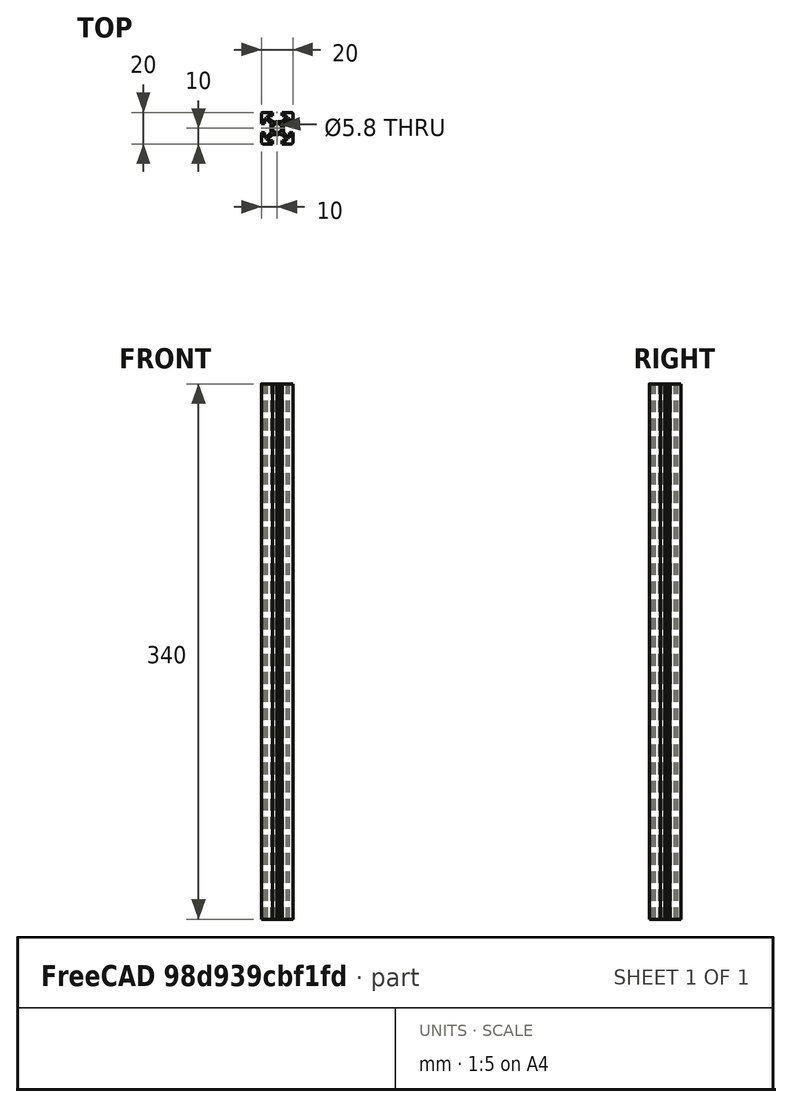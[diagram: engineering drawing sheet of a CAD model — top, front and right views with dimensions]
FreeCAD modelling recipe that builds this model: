
FCSTD DOCUMENT  (FreeCAD 0.17R13387 (Git))
Label: X-Profile_2020
License: All rights reserved
LicenseURL: http://en.wikipedia.org/wiki/All_rights_reserved
objects: Sketcher::SketchObject×1, PartDesign::Pad×1, PartDesign::Body×1
note: 4 computed .brp shape members not serialized (recipe doc carries the construction recipe); baked Part::Feature solids carry a one-line shape summary decoded from their .brp

FEATURE [Sketcher::SketchObject] Sketch001
  sketch-geometry (77):
    g0: LineSegment StartX=-8 StartY=-3 StartZ=0 EndX=-10 EndY=-3 EndZ=0
    g1: LineSegment StartX=-10 StartY=-3 StartZ=0 EndX=-10 EndY=-9 EndZ=0
    g2: ArcOfCircle CenterX=-9 CenterY=-9 CenterZ=0 NormalX=0 NormalY=0 NormalZ=1 AngleXU=0 Radius=1 StartAngle=3.14159 EndAngle=4.71239
    g3: LineSegment StartX=-9 StartY=-10 StartZ=0 EndX=-3 EndY=-10 EndZ=0
    g4: LineSegment StartX=-3 StartY=-10 StartZ=0 EndX=-3 EndY=-8 EndZ=0
    g5: LineSegment StartX=-3 StartY=-8 StartZ=0 EndX=-6 EndY=-8 EndZ=0
    g6: LineSegment StartX=-6 StartY=-8 StartZ=0 EndX=-6 EndY=-7.06066 EndZ=0
    g7: LineSegment StartX=-6 StartY=-7.06066 StartZ=0 EndX=-2.93934 EndY=-4 EndZ=0
    g8: LineSegment StartX=-2.93934 StartY=-4 StartZ=0 EndX=-0.65359 EndY=-4 EndZ=0
    g9: ArcOfCircle CenterX=-0.65359 CenterY=-3.5 CenterZ=0 NormalX=0 NormalY=0 NormalZ=1 AngleXU=0 Radius=0.5 StartAngle=4.71239 EndAngle=5.23599
    g10: LineSegment StartX=-0.40359 StartY=-3.93301 StartZ=0 EndX=0 EndY=-3.7 EndZ=0
    g11: LineSegment StartX=0 StartY=-3.7 StartZ=0 EndX=0.40359 EndY=-3.93301 EndZ=0
    g12: ArcOfCircle CenterX=0.65359 CenterY=-3.5 CenterZ=0 NormalX=0 NormalY=0 NormalZ=1 AngleXU=0 Radius=0.5 StartAngle=4.18879 EndAngle=5.23599
    g13: LineSegment StartX=0.90359 StartY=-3.93301 StartZ=0 EndX=1.21889 EndY=-3.75098 EndZ=0
    g14: LineSegment StartX=1.21889 StartY=-3.75098 StartZ=0 EndX=2.5 EndY=-4 EndZ=0
    g15: LineSegment StartX=2.5 StartY=-4 StartZ=0 EndX=2.93934 EndY=-4 EndZ=0
    g16: LineSegment StartX=2.93934 StartY=-4 StartZ=0 EndX=6 EndY=-7.06066 EndZ=0
    g17: LineSegment StartX=6 StartY=-7.06066 StartZ=0 EndX=6 EndY=-8 EndZ=0
    g18: LineSegment StartX=6 StartY=-8 StartZ=0 EndX=3 EndY=-8 EndZ=0
    g19: LineSegment StartX=3 StartY=-8 StartZ=0 EndX=3 EndY=-10 EndZ=0
    g20: LineSegment StartX=3 StartY=-10 StartZ=0 EndX=9 EndY=-10 EndZ=0
    g21: ArcOfCircle CenterX=9 CenterY=-9 CenterZ=0 NormalX=0 NormalY=0 NormalZ=1 AngleXU=0 Radius=1 StartAngle=4.71239 EndAngle=6.28319
    g22: LineSegment StartX=10 StartY=-9 StartZ=0 EndX=10 EndY=-3 EndZ=0
    g23: LineSegment StartX=10 StartY=-3 StartZ=0 EndX=8 EndY=-3 EndZ=0
    g24: LineSegment StartX=8 StartY=-3 StartZ=0 EndX=8 EndY=-6 EndZ=0
    g25: LineSegment StartX=8 StartY=-6 StartZ=0 EndX=7.06066 EndY=-6 EndZ=0
    g26: LineSegment StartX=7.06066 StartY=-6 StartZ=0 EndX=4 EndY=-2.93934 EndZ=0
    g27: LineSegment StartX=4 StartY=-2.93934 StartZ=0 EndX=4 EndY=-0.65359 EndZ=0
    g28: ArcOfCircle CenterX=3.5 CenterY=-0.65359 CenterZ=0 NormalX=0 NormalY=0 NormalZ=1 AngleXU=0 Radius=0.5 StartAngle=0 EndAngle=0.523599
    g29: LineSegment StartX=3.93301 StartY=-0.40359 StartZ=0 EndX=3.7 EndY=0 EndZ=0
    g30: LineSegment StartX=3.7 StartY=0 StartZ=0 EndX=3.93301 EndY=0.40359 EndZ=0
    g31: ArcOfCircle CenterX=3.5 CenterY=0.65359 CenterZ=0 NormalX=0 NormalY=0 NormalZ=1 AngleXU=0 Radius=0.5 StartAngle=5.75959 EndAngle=6.80678
    g32: LineSegment StartX=3.93301 StartY=0.90359 StartZ=0 EndX=3.75098 EndY=1.21889 EndZ=0
    g33: LineSegment StartX=3.75098 StartY=1.21889 StartZ=0 EndX=4 EndY=2.5 EndZ=0
    g34: LineSegment StartX=4 StartY=2.5 StartZ=0 EndX=4 EndY=2.93934 EndZ=0
    g35: LineSegment StartX=4 StartY=2.93934 StartZ=0 EndX=7.06066 EndY=6 EndZ=0
    g36: LineSegment StartX=7.06066 StartY=6 StartZ=0 EndX=8 EndY=6 EndZ=0
    g37: LineSegment StartX=8 StartY=6 StartZ=0 EndX=8 EndY=3 EndZ=0
    g38: LineSegment StartX=8 StartY=3 StartZ=0 EndX=10 EndY=3 EndZ=0
    g39: LineSegment StartX=10 StartY=3 StartZ=0 EndX=10 EndY=9 EndZ=0
    g40: ArcOfCircle CenterX=9 CenterY=9 CenterZ=0 NormalX=0 NormalY=0 NormalZ=1 AngleXU=0 Radius=1 StartAngle=0 EndAngle=1.5708
    g41: LineSegment StartX=9 StartY=10 StartZ=0 EndX=3 EndY=10 EndZ=0
    g42: LineSegment StartX=3 StartY=10 StartZ=0 EndX=3 EndY=8 EndZ=0
    g43: LineSegment StartX=3 StartY=8 StartZ=0 EndX=6 EndY=8 EndZ=0
    g44: LineSegment StartX=6 StartY=8 StartZ=0 EndX=6 EndY=7.06066 EndZ=0
    g45: LineSegment StartX=6 StartY=7.06066 StartZ=0 EndX=2.93934 EndY=4 EndZ=0
    g46: LineSegment StartX=2.93934 StartY=4 StartZ=0 EndX=0.65359 EndY=4 EndZ=0
    g47: ArcOfCircle CenterX=0.65359 CenterY=3.5 CenterZ=0 NormalX=0 NormalY=0 NormalZ=1 AngleXU=0 Radius=0.5 StartAngle=1.5708 EndAngle=2.0944
    g48: LineSegment StartX=0.40359 StartY=3.93301 StartZ=0 EndX=0 EndY=3.7 EndZ=0
    g49: LineSegment StartX=0 StartY=3.7 StartZ=0 EndX=-0.40359 EndY=3.93301 EndZ=0
    g50: ArcOfCircle CenterX=-0.65359 CenterY=3.5 CenterZ=0 NormalX=0 NormalY=0 NormalZ=1 AngleXU=0 Radius=0.5 StartAngle=1.0472 EndAngle=2.0944
    g51: LineSegment StartX=-0.90359 StartY=3.93301 StartZ=0 EndX=-1.21889 EndY=3.75098 EndZ=0
    g52: LineSegment StartX=-1.21889 StartY=3.75098 StartZ=0 EndX=-2.5 EndY=4 EndZ=0
    g53: LineSegment StartX=-2.5 StartY=4 StartZ=0 EndX=-2.93934 EndY=4 EndZ=0
    g54: LineSegment StartX=-2.93934 StartY=4 StartZ=0 EndX=-6 EndY=7.06066 EndZ=0
    g55: LineSegment StartX=-6 StartY=7.06066 StartZ=0 EndX=-6 EndY=8 EndZ=0
    g56: LineSegment StartX=-6 StartY=8 StartZ=0 EndX=-3 EndY=8 EndZ=0
    g57: LineSegment StartX=-3 StartY=8 StartZ=0 EndX=-3 EndY=10 EndZ=0
    g58: LineSegment StartX=-3 StartY=10 StartZ=0 EndX=-9 EndY=10 EndZ=0
    g59: ArcOfCircle CenterX=-9 CenterY=9 CenterZ=0 NormalX=0 NormalY=0 NormalZ=1 AngleXU=0 Radius=1 StartAngle=1.5708 EndAngle=3.14159
    g60: LineSegment StartX=-10 StartY=9 StartZ=0 EndX=-10 EndY=3 EndZ=0
    g61: LineSegment StartX=-10 StartY=3 StartZ=0 EndX=-8 EndY=3 EndZ=0
    g62: LineSegment StartX=-8 StartY=3 StartZ=0 EndX=-8 EndY=6 EndZ=0
    g63: LineSegment StartX=-8 StartY=6 StartZ=0 EndX=-7.06066 EndY=6 EndZ=0
    g64: LineSegment StartX=-7.06066 StartY=6 StartZ=0 EndX=-4 EndY=2.93934 EndZ=0
    g65: LineSegment StartX=-4 StartY=2.93934 StartZ=0 EndX=-4 EndY=0.65359 EndZ=0
    g66: ArcOfCircle CenterX=-3.5 CenterY=0.65359 CenterZ=0 NormalX=0 NormalY=0 NormalZ=1 AngleXU=0 Radius=0.5 StartAngle=3.14159 EndAngle=3.66519
    g67: LineSegment StartX=-3.93301 StartY=0.40359 StartZ=0 EndX=-3.7 EndY=0 EndZ=0
    g68: LineSegment StartX=-3.7 StartY=0 StartZ=0 EndX=-3.93301 EndY=-0.40359 EndZ=0
    g69: ArcOfCircle CenterX=-3.5 CenterY=-0.65359 CenterZ=0 NormalX=0 NormalY=0 NormalZ=1 AngleXU=0 Radius=0.5 StartAngle=2.61799 EndAngle=3.66519
    g70: LineSegment StartX=-3.93301 StartY=-0.90359 StartZ=0 EndX=-3.75098 EndY=-1.21889 EndZ=0
    g71: LineSegment StartX=-3.75098 StartY=-1.21889 StartZ=0 EndX=-4 EndY=-2.5 EndZ=0
    g72: LineSegment StartX=-4 StartY=-2.5 StartZ=0 EndX=-4 EndY=-2.93934 EndZ=0
    g73: LineSegment StartX=-4 StartY=-2.93934 StartZ=0 EndX=-7.06066 EndY=-6 EndZ=0
    g74: LineSegment StartX=-7.06066 StartY=-6 StartZ=0 EndX=-8 EndY=-6 EndZ=0
    g75: LineSegment StartX=-8 StartY=-6 StartZ=0 EndX=-8 EndY=-3 EndZ=0
    g76: Circle CenterX=0 CenterY=0 CenterZ=0 NormalX=0 NormalY=0 NormalZ=1 AngleXU=0 Radius=2.9
  constraints (105):
    c: Horizontal(g0)
    c: Coincident(g0,g1)
    c: Vertical(g1)
    c: Coincident(g1,g2)
    c: Coincident(g2,g3)
    c: Horizontal(g3)
    c: Coincident(g3,g4)
    c: Coincident(g4,g5)
    c: Horizontal(g5)
    c: Coincident(g5,g6)
    c: Coincident(g6,g7)
    c: Coincident(g7,g8)
    c: Horizontal(g8)
    c: Coincident(g8,g9)
    c: Coincident(g9,g10)
    c: Coincident(g10,g11)
    c: Coincident(g11,g12)
    c: Coincident(g12,g13)
    c: Coincident(g13,g14)
    c: Coincident(g14,g15)
    c: Horizontal(g15)
    c: Coincident(g15,g16)
    c: Coincident(g16,g17)
    c: Coincident(g17,g18)
    c: Coincident(g18,g19)
    c: Vertical(g19)
    c: Coincident(g19,g20)
    c: Horizontal(g20)
    c: Coincident(g20,g21)
    c: Coincident(g21,g22)
    c: Vertical(g22)
    c: Coincident(g22,g23)
    c: Horizontal(g23)
    c: Coincident(g23,g24)
    c: Vertical(g24)
    c: Coincident(g24,g25)
    c: Coincident(g25,g26)
    c: Coincident(g26,g27)
    c: Vertical(g27)
    c: Coincident(g27,g28)
    c: Coincident(g28,g29)
    c: Coincident(g29,g30)
    c: Coincident(g30,g31)
    c: Coincident(g31,g32)
    c: Coincident(g32,g33)
    c: Coincident(g33,g34)
    c: Vertical(g34)
    c: Coincident(g34,g35)
    c: Coincident(g35,g36)
    c: Coincident(g36,g37)
    c: Coincident(g37,g38)
    c: Horizontal(g38)
    c: Coincident(g38,g39)
    c: Vertical(g39)
    c: Coincident(g39,g40)
    c: Coincident(g40,g41)
    c: Horizontal(g41)
    c: Coincident(g41,g42)
    c: Coincident(g42,g43)
    c: Horizontal(g43)
    c: Coincident(g43,g44)
    c: Coincident(g44,g45)
    c: Coincident(g45,g46)
    c: Horizontal(g46)
    c: Coincident(g46,g47)
    c: Coincident(g47,g48)
    c: Coincident(g48,g49)
    c: Coincident(g49,g50)
    c: Coincident(g50,g51)
    c: Coincident(g51,g52)
    c: Coincident(g52,g53)
    c: Horizontal(g53)
    c: Coincident(g53,g54)
    c: Coincident(g54,g55)
    c: Vertical(g55)
    c: Coincident(g55,g56)
    c: Coincident(g56,g57)
    c: Vertical(g57)
    c: Coincident(g57,g58)
    c: Horizontal(g58)
    c: Coincident(g58,g59)
    c: Coincident(g59,g60)
    c: Vertical(g60)
    c: Coincident(g60,g61)
    c: Horizontal(g61)
    c: Coincident(g61,g62)
    c: Vertical(g62)
    c: Coincident(g62,g63)
    c: Horizontal(g63)
    c: Coincident(g63,g64)
    c: Coincident(g64,g65)
    c: Vertical(g65)
    c: Coincident(g65,g66)
    c: Coincident(g66,g67)
    c: Coincident(g67,g68)
    c: Coincident(g68,g69)
    c: Coincident(g69,g70)
    c: Coincident(g70,g71)
    c: Coincident(g71,g72)
    c: Vertical(g72)
    c: Coincident(g72,g73)
    c: Coincident(g73,g74)
    c: Coincident(g74,g75)
    c: Coincident(g75,g0)
    c: Radius(g76) = 2.9
FEATURE [PartDesign::Pad] Pad
  Length = 340
  Length2 = 100
  Midplane = true
  Profile = -> Sketch001
  Type = 0
FEATURE [PartDesign::Body] Body
  Group = -> [Sketch001,Pad]
  Origin = -> Origin
  Tip = -> Pad
